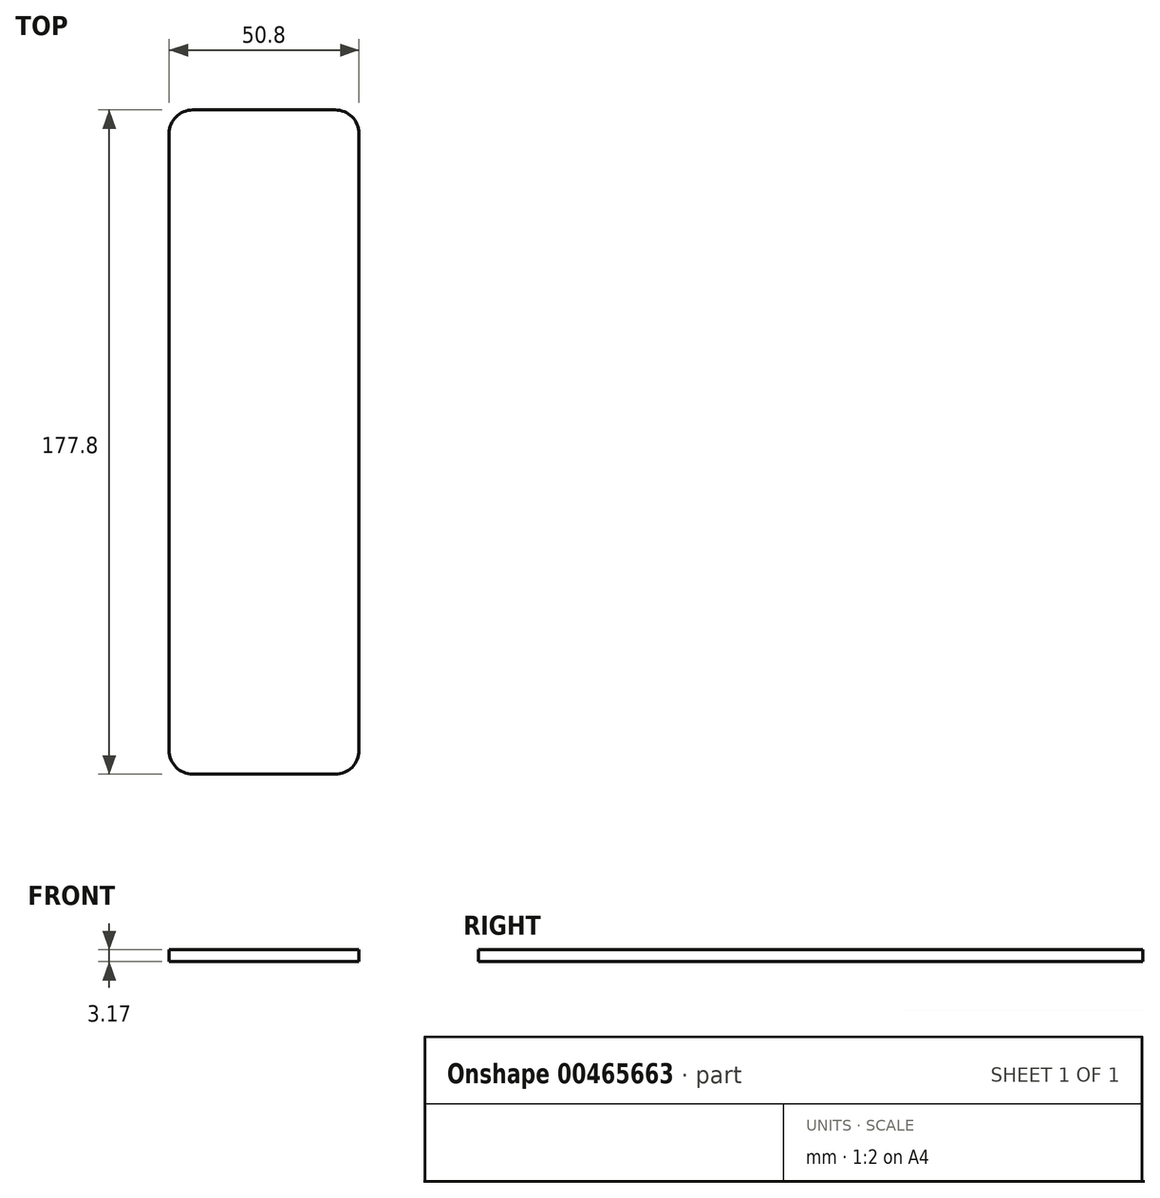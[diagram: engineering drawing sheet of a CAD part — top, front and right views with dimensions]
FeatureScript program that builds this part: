
annotation { "Feature Type Name" : "Feature", "Feature Type Description" : "" }
export const myFeature = defineFeature(function(context is Context, id is Id, definition is map)
    precondition{}
    {
        {
            var Q0;
            Q0=qCreatedBy(makeId("Top.planeOp"),FACE);
            var sketch = newSketch(context, id + "F0", { "sketchPlane" : qUnion([Q0])});
            skLineSegment(sketch, "E0.bottom", {"start": v(6.35, 0) * mm, "end": v(44.45, 0) * mm});
            skLineSegment(sketch, "E0.top", {"start": v(6.35, 177.8) * mm, "end": v(44.45, 177.8) * mm});
            skLineSegment(sketch, "E0.left", {"start": v(0, 6.35) * mm, "end": v(0, 171.45) * mm});
            skLineSegment(sketch, "E0.right", {"start": v(50.8, 6.35) * mm, "end": v(50.8, 171.45) * mm});
            skPoint(sketch, "E1.visualSharp", {"position": v(0, 177.8) * mm});
            skArc(sketch, "E1.filletArc", {"start": v(6.35, 177.8) * mm, "mid": v(1.86, 175.94) * mm, "end": v(0, 171.45) * mm});
            skPoint(sketch, "E2.visualSharp", {"position": v(50.8, 177.8) * mm});
            skArc(sketch, "E2.filletArc", {"start": v(50.8, 171.45) * mm, "mid": v(48.94, 175.94) * mm, "end": v(44.45, 177.8) * mm});
            skPoint(sketch, "E3.visualSharp", {"position": v(50.8, 0) * mm});
            skArc(sketch, "E3.filletArc", {"start": v(44.45, 0) * mm, "mid": v(48.94, 1.86) * mm, "end": v(50.8, 6.35) * mm});
            skPoint(sketch, "E4.visualSharp", {"position": v(0, 0) * mm});
            skArc(sketch, "E4.filletArc", {"start": v(0, 6.35) * mm, "mid": v(1.86, 1.86) * mm, "end": v(6.35, 0) * mm});
            skSolve(sketch);
        }
        {
            var Q0;
            Q0=qSketchRegion(id+"F0",true);
            extrude(context, id + "F1", {"entities" : qUnion([Q0]), "depth" : 3.17 * mm});
        }
    });
